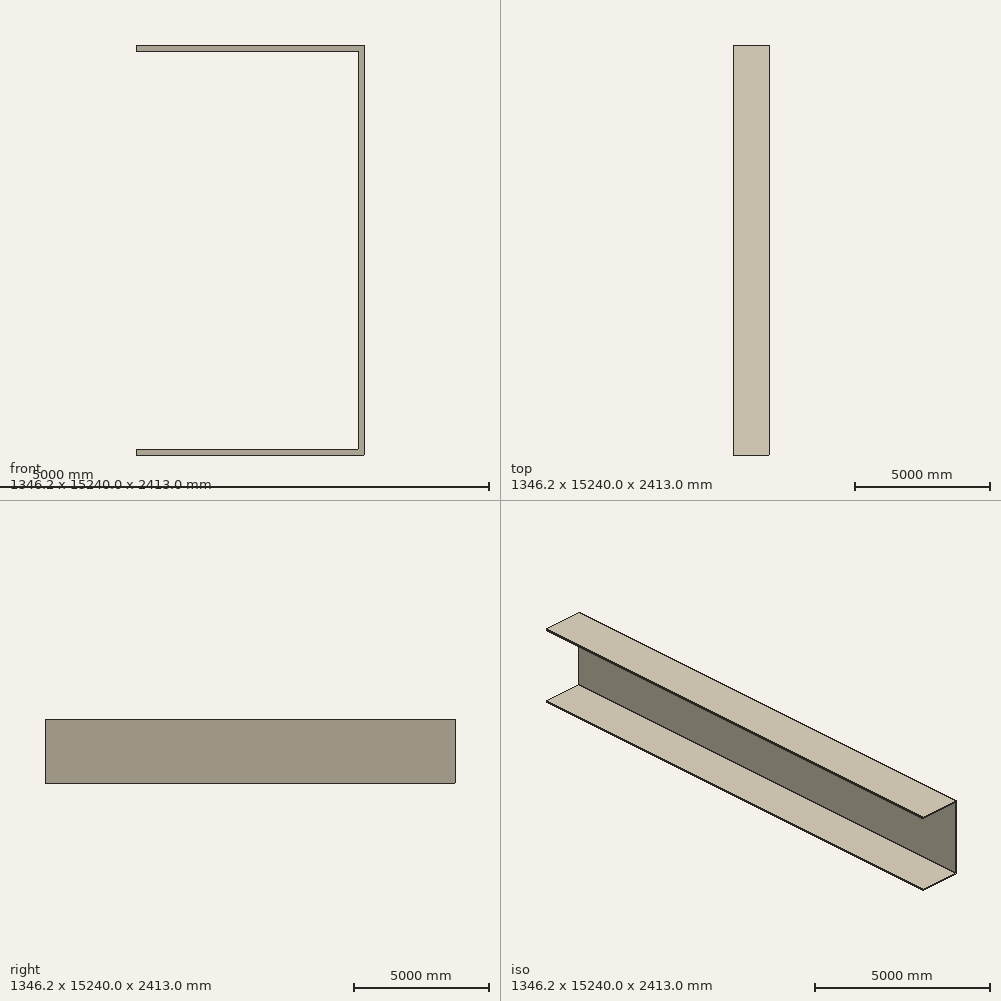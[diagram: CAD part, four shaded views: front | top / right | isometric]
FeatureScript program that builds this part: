
annotation { "Feature Type Name" : "Feature", "Feature Type Description" : "" }
export const myFeature = defineFeature(function(context is Context, id is Id, definition is map)
    precondition{}
    {
        {
            var Q0;
            Q0=qCreatedBy(makeId("Front.planeOp"),FACE);
            var sketch = newSketch(context, id + "F0", { "sketchPlane" : qUnion([Q0])});
            skLineSegment(sketch, "E0", {"start": v(1346.2, 1206.5) * mm, "end": v(1346.2, -1206.5) * mm});
            skLineSegment(sketch, "E1", {"start": v(1346.2, -1206.5) * mm, "end": v(0, -1206.5) * mm});
            skLineSegment(sketch, "E2", {"start": v(1346.2, 1206.5) * mm, "end": v(0, 1206.5) * mm});
            skLineSegment(sketch, "E3", {"start": v(0, 1206.5) * mm, "end": v(0, 1168.4) * mm});
            skLineSegment(sketch, "E4", {"start": v(0, 1168.4) * mm, "end": v(1308.1, 1168.4) * mm});
            skLineSegment(sketch, "E5", {"start": v(1308.1, 1168.4) * mm, "end": v(1308.1, -1168.4) * mm});
            skLineSegment(sketch, "E6", {"start": v(0, -1206.5) * mm, "end": v(0, -1168.4) * mm});
            skLineSegment(sketch, "E7", {"start": v(0, -1168.4) * mm, "end": v(1308.1, -1168.4) * mm});
            skSolve(sketch);
        }
        {
            var Q0;
            Q0 = qSketchRegion(id + "F0", true);
            extrude(context, id + "F1", {"entities" : qUnion([Q0]), "depth" : 15240 * mm});
        }
    });
